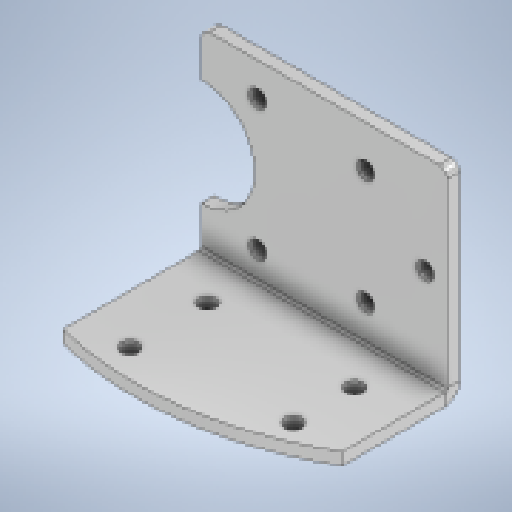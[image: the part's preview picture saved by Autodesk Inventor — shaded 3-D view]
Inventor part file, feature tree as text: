
AUTODESK INVENTOR PART (.ipt)
format: ipt  version: 2024.2 (Build 282272000, 272)  size: 212,480 bytes
history: native  units: in
note: dims shown in document units (in); Inventor stores cm internally (conversion verified against a paired STEP export)
features: other x8, reference x7, sketch x6, sheet_metal_op x4, hole x2, chamfer x1
ambient origin geometry x8: Origin, YZ Plane, XZ Plane, XY Plane, X Axis, Y Axis, Z Axis, Center Point
bodies: Solid1 (feature_tree)
feature tree (28):
  sheet_metal_op  "Face1"
  hole  "Hole2"  [1 undecoded]
  sheet_metal_op  "Flange2"
  chamfer  "Corner Round1"
  hole  "Hole3"  [1 undecoded]
  sketch  "Sketch1"  dims[d0=1.185in d1=0.9843in]
  other  "Plate1"
  sketch  "Sketch6"  dims[d2=0.0591in]
  reference  "Reference19"
  reference  "Reference20"
  reference  "Reference21"
  reference  "Reference22"
  reference  "Reference23"
  sketch  "Sketch7"  dims[d20=0.0827in d21=0.2362in d22=0.1575in d23=0.0787in d24=90.0deg d25=0.315in d26=0.8108in d27=0.0591in]
  reference  "Reference24"
  sketch  "Sketch8"  dims[d28=0.0in]
  other  "Plate3"
  sheet_metal_op  "Bend2"
  sheet_metal_op  "Corner2"
  sketch  "Sketch9"  dims[d29=0.0591in]
  reference  "Reference25"
  sketch  "Sketch10"  dims[d30=0.0295in d31=0.1181in d32=0.0122in d33=0.7874in d34=90.0deg d35=0.0122in d36=0.2362in d37=0.0591in d38=0.0122in d39=0.3937in d40=0.0591in d41=0.0in d42=0.0059in d43=0.0394in d44=0.7087in d45=0.374in d46=0.2953in d47=0.1969in d48=0.0827in d49=0.2362in d50=0.1575in d51=0.0787in d52=90.0deg d53=0.315in d54=0.8108in]
  other  "Cut1"
  other  "Cut2"
  other  "2_Arm.iam"
  other  "HTD-45H:2"
  other  "HTD-45H:1"
  other  "axis_2_bottom_frame:1"
note: 2 required parameter values undecoded (feature->parameter linkage not recoverable at this tier; creation-order binding heuristic only, values carry confidence <= 0.55)
